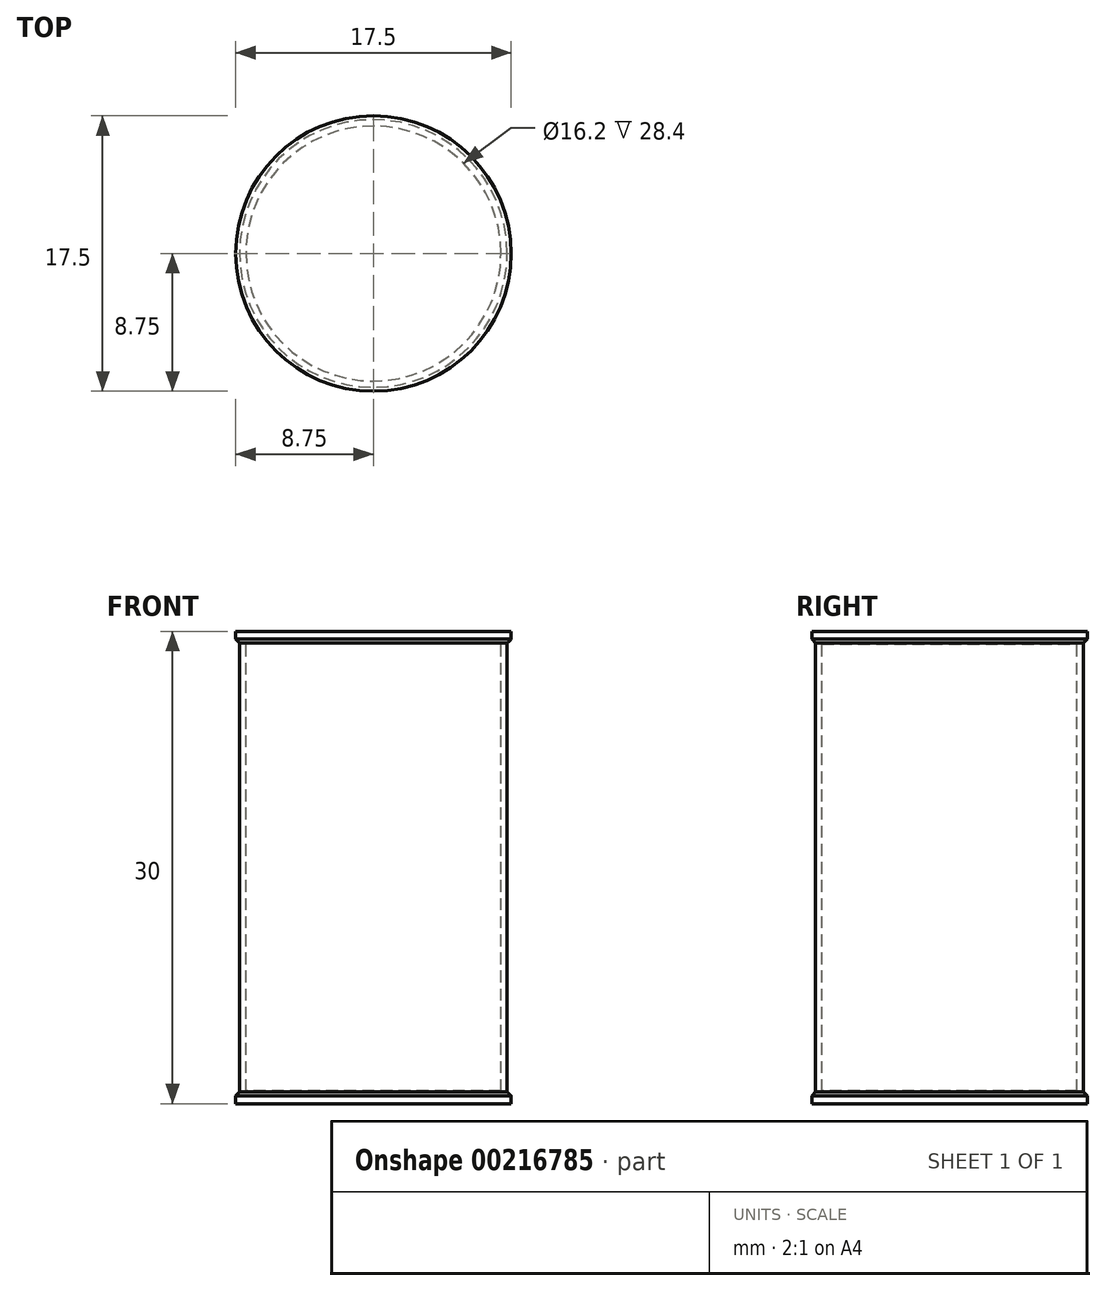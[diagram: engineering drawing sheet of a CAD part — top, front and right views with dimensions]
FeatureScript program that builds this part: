
annotation { "Feature Type Name" : "Feature", "Feature Type Description" : "" }
export const myFeature = defineFeature(function(context is Context, id is Id, definition is map)
    precondition{}
    {
        {
            var Q0;
            Q0=qCreatedBy(makeId("Front.planeOp"),FACE);
            var sketch = newSketch(context, id + "F0", { "sketchPlane" : qUnion([Q0])});
            skLineSegment(sketch, "E0", {"start": v(0, 30) * mm, "end": v(8.5, 30) * mm});
            skLineSegment(sketch, "E1", {"start": v(8.5, 30) * mm, "end": v(8.5, 0) * mm});
            skLineSegment(sketch, "E2", {"start": v(8.5, 0) * mm, "end": v(0, 0) * mm});
            skLineSegment(sketch, "E3", {"start": v(8.5, 30) * mm, "end": v(8.75, 30) * mm});
            skLineSegment(sketch, "E4", {"start": v(8.75, 30) * mm, "end": v(8.75, 29.5) * mm});
            skLineSegment(sketch, "E5", {"start": v(8.75, 29.5) * mm, "end": v(8.5, 29.25) * mm});
            skLineSegment(sketch, "E6", {"start": v(0, 15) * mm, "end": v(8.5, 15) * mm, "construction": true});
            skLineSegment(sketch, "E7.MirrorCS", {"start": v(8.5, 0) * mm, "end": v(8.75, 0) * mm});
            skLineSegment(sketch, "E8.MirrorCS", {"start": v(8.5, 0) * mm, "end": v(8.5, 30) * mm});
            skLineSegment(sketch, "E9.MirrorCS", {"start": v(8.75, 0.5) * mm, "end": v(8.5, 0.75) * mm});
            skLineSegment(sketch, "E10.MirrorCS", {"start": v(8.75, 0) * mm, "end": v(8.75, 0.5) * mm});
            skLineSegment(sketch, "E11", {"start": v(0, 30) * mm, "end": v(0, 0) * mm});
            skLineSegment(sketch, "E12", {"start": v(0, 29.2) * mm, "end": v(8.1, 29.2) * mm});
            skLineSegment(sketch, "E13", {"start": v(8.1, 29.2) * mm, "end": v(8.1, 15) * mm});
            skLineSegment(sketch, "E14.MirrorCS", {"start": v(0, 0.8) * mm, "end": v(8.1, 0.8) * mm});
            skLineSegment(sketch, "E15.MirrorCS", {"start": v(8.1, 0.8) * mm, "end": v(8.1, 15) * mm});
            skSolve(sketch);
        }
        {
            var Q0;
            {var subQ0=sQuery(id+"F0.wireOp",EDGE,"E3");Q0=makeQuery(id+"F0.imprint","IMPRINT",FACE,{"disambiguationData":[TD([[makeQuery(id+"F0.imprint","IMPRINT",EDGE,{"derivedFrom":subQ0}),-1.0]])]});}
            var Q1;
            {var subQ0=sQuery(id+"F0.wireOp",EDGE,"E7.MirrorCS");Q1=makeQuery(id+"F0.imprint","IMPRINT",FACE,{"disambiguationData":[TD([[makeQuery(id+"F0.imprint","IMPRINT",EDGE,{"derivedFrom":subQ0}),1.0]])]});}
            var Q2;
            {var subQ2=sQuery(id+"F0.wireOp",EDGE,"E0");Q2=makeQuery(id+"F0.imprint","IMPRINT",FACE,{"disambiguationData":[TD([[makeQuery(id+"F0.imprint","IMPRINT",EDGE,{"derivedFrom":subQ2}),-1.0]])]});}
            var Q3;
            Q3=sQuery(id+"F0.wireOp",EDGE,"E11");
            revolve(context, id + "F1", {"entities" : qUnion([Q0, Q1, Q2]), "axis" : qUnion([Q3]), "revolveType" : RevolveType.FULL});
        }
    });
